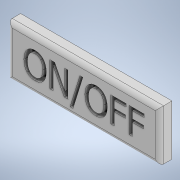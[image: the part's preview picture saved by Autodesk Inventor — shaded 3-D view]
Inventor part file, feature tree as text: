
AUTODESK INVENTOR PART (.ipt)
format: ipt  version: 2021.2 (Build 252289000, 289)  size: 195,584 bytes
history: native  units: in
note: dims shown in document units (in); Inventor stores cm internally (conversion verified against a paired STEP export)
features: extrude x2, sketch x2, fillet x1
ambient origin geometry x8: Origin, YZ Plane, XZ Plane, XY Plane, X Axis, Y Axis, Z Axis, Center Point
bodies: Solid1 (feature_tree)
feature tree (5):
  extrude  "Extrusion1"  Depth=0.75in
  sketch  "Sketch2"  dims[d2=0.1875in d3=0.0in d13=0.125in d14=0.0in d15=0.0625in]
  extrude  "Extrusion2"  TaperAngle=0.0deg  [1 undecoded]
  fillet  "Fillet1"  Radius=0.125in
  sketch  "Sketch1"  dims[d0=2.25in d1=0.75in]
note: 1 required parameter value undecoded (feature->parameter linkage not recoverable at this tier; creation-order binding heuristic only, values carry confidence <= 0.55)
